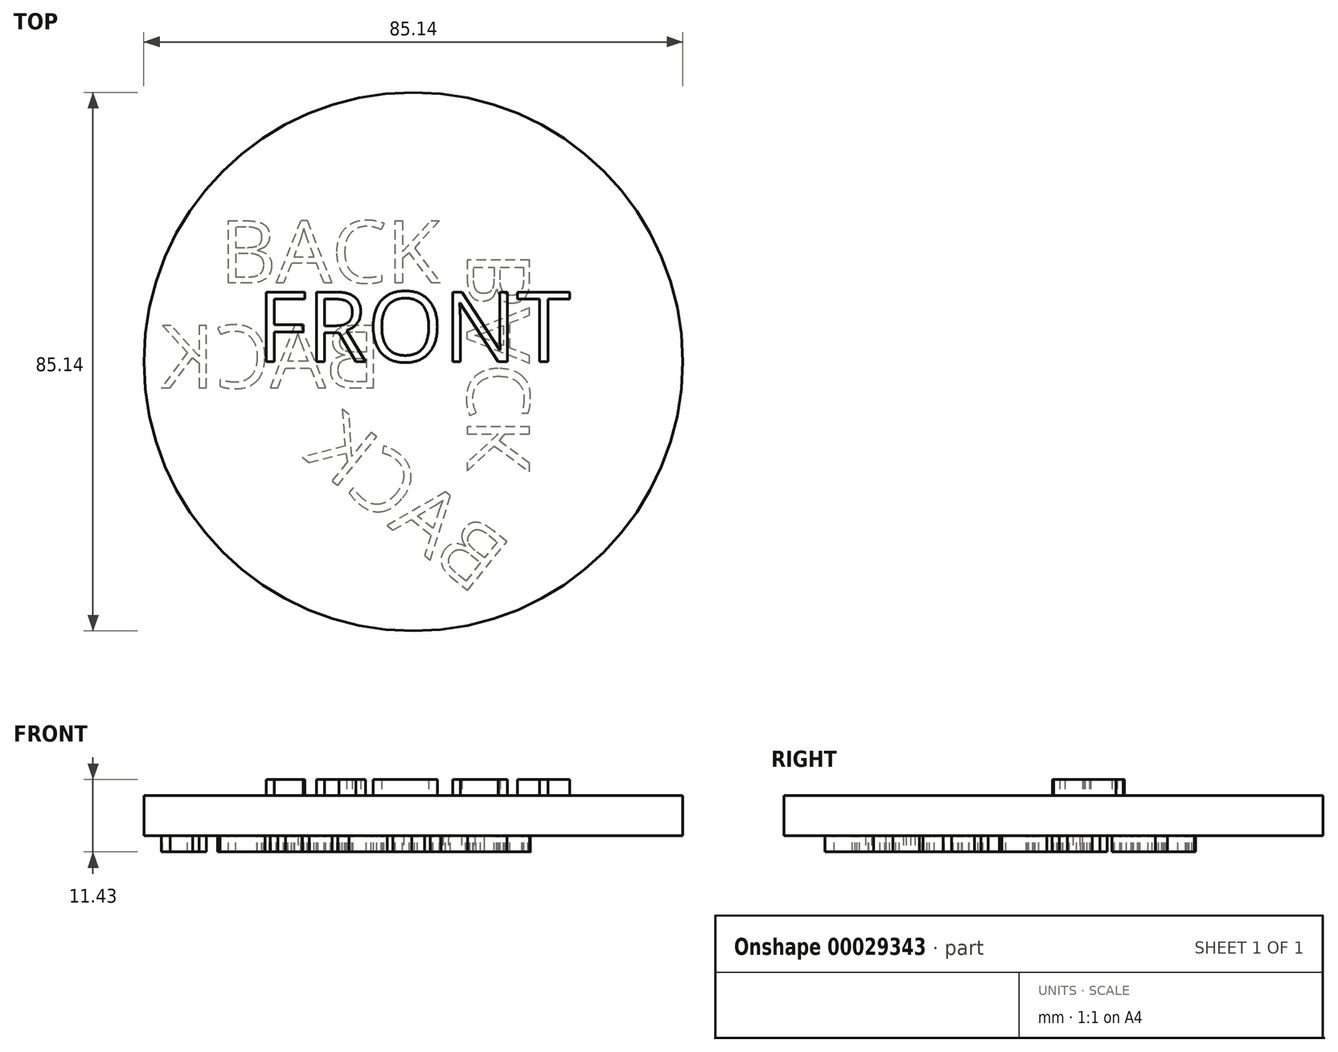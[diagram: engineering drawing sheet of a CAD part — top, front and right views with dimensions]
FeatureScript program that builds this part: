
annotation { "Feature Type Name" : "Feature", "Feature Type Description" : "" }
export const myFeature = defineFeature(function(context is Context, id is Id, definition is map)
    precondition{}
    {
        {
            var Q0;
            Q0=qCreatedBy(makeId("Top.planeOp"),FACE);
            var sketch = newSketch(context, id + "F0", { "sketchPlane" : qUnion([Q0])});
            skCircle(sketch, "E0", {"center": v(0, 0) * mm, "radius": 42.57 * mm});
            skSolve(sketch);
        }
        {
            var Q0;
            Q0=makeQuery(id+"F0.imprint","IMPRINT",FACE,{"disambiguationData":[TD([[makeQuery(id+"F0.imprint","IMPRINT",EDGE,{"derivedFrom":sQuery(id+"F0.wireOp",EDGE,"E0")}),1.0]])]});
            extrude(context, id + "F1", {"entities" : qUnion([Q0]), "depth" : 6.35 * mm});
        }
        {
            var Q0;
            Q0=makeQuery(id+"F1.opExtrude","CAP_FACE",FACE,{"disambiguationData":[OSD([sQuery(id+"F0.wireOp",EDGE,"E0")])],"isStart":false});
            var sketch = newSketch(context, id + "F2", { "sketchPlane" : qUnion([Q0])});
            skText(sketch, "E1", { "text": "FRONT", "fontName": "OpenSans-Regular.ttf"});
            const initialGuessF2  = {"E1": [-0.02476, 0, 1, 0, 0.0111]};
            skSetInitialGuess(sketch, initialGuessF2);
            skSolve(sketch);
        }
        {
            var Q0;
            Q0=qSketchRegion(id+"F2",true);
            extrude(context, id + "F3", {"entities" : qUnion([Q0]), "operationType" : NewBodyOperationType.ADD, "depth" : 2.54 * mm});
        }
        {
            var Q0;
            Q0=makeQuery(id+"F1.opExtrude","CAP_FACE",FACE,{"disambiguationData":[OSD([sQuery(id+"F0.wireOp",EDGE,"E0")])],"isStart":true});
            var sketch = newSketch(context, id + "F4", { "sketchPlane" : qUnion([Q0])});
            skText(sketch, "E2", { "text": "BACK", "fontName": "OpenSans-Regular.ttf"});
            skText(sketch, "E3", { "text": "BACK", "fontName": "OpenSans-Regular.ttf"});
            skText(sketch, "E4", { "text": "BACK", "fontName": "OpenSans-Regular.ttf"});
            const initialGuessF4  = {"E2": [-0.00492, 0.00414, -1, 0, 0.00994], "E3": [0.01838, -0.01744, 0, 1, 0.00994], "E4": [0.00965, 0.03698, -0.77875, -0.62733, 0.00994]};
            skSetInitialGuess(sketch, initialGuessF4);
            skSolve(sketch);
        }
        {
            var Q0;
            Q0=qSketchRegion(id+"F4",true);
            extrude(context, id + "F5", {"entities" : qUnion([Q0]), "operationType" : NewBodyOperationType.ADD, "depth" : 2.54 * mm});
        }
        {
            var Q0;
            {var subQ0=sQuery(id+"F0.wireOp",EDGE,"E0");Q0=makeQuery(id+"F3.boolean.opBoolean","SPLIT",FACE,{"disambiguationData":[TD([makeQuery(id+"F1.opExtrude","SWEPT_FACE",FACE,{"disambiguationData":[OSD([subQ0])]})])],"derivedFrom":makeQuery(id+"F1.opExtrude","CAP_FACE",FACE,{"disambiguationData":[OSD([subQ0])],"isStart":false})});}
            var sketch = newSketch(context, id + "F6", { "sketchPlane" : qUnion([Q0])});
            skText(sketch, "E5", { "text": "BACK\n", "fontName": "OpenSans-Regular.ttf"});
            const initialGuessF6  = {"E5": [-0.03058, 0.01242, 1, 0, 0.00994]};
            skSetInitialGuess(sketch, initialGuessF6);
            skSolve(sketch);
        }
        {
            var Q0;
            Q0 = qSketchRegion(id + "F6", true);
            var Q1;
            Q1=makeQuery(id+"F5.opExtrude","CAP_FACE",FACE,{"disambiguationData":[OSD([sQuery(id+"F4.wireOp",EDGE,"E2.sketch_text.stroke-0"),sQuery(id+"F4.wireOp",EDGE,"E2.sketch_text.stroke-1"),sQuery(id+"F4.wireOp",EDGE,"E2.sketch_text.stroke-2"),sQuery(id+"F4.wireOp",EDGE,"E2.sketch_text.stroke-3"),sQuery(id+"F4.wireOp",EDGE,"E2.sketch_text.stroke-4"),sQuery(id+"F4.wireOp",EDGE,"E2.sketch_text.stroke-5"),sQuery(id+"F4.wireOp",EDGE,"E2.sketch_text.stroke-6"),sQuery(id+"F4.wireOp",EDGE,"E2.sketch_text.stroke-7"),sQuery(id+"F4.wireOp",EDGE,"E2.sketch_text.stroke-8"),sQuery(id+"F4.wireOp",EDGE,"E2.sketch_text.stroke-9"),sQuery(id+"F4.wireOp",EDGE,"E2.sketch_text.stroke-10"),sQuery(id+"F4.wireOp",EDGE,"E2.sketch_text.stroke-11"),sQuery(id+"F4.wireOp",EDGE,"E2.sketch_text.stroke-12"),sQuery(id+"F4.wireOp",EDGE,"E2.sketch_text.stroke-13"),sQuery(id+"F4.wireOp",EDGE,"E2.sketch_text.stroke-14"),sQuery(id+"F4.wireOp",EDGE,"E2.sketch_text.stroke-15"),sQuery(id+"F4.wireOp",EDGE,"E2.sketch_text.stroke-16"),sQuery(id+"F4.wireOp",EDGE,"E2.sketch_text.stroke-17"),sQuery(id+"F4.wireOp",EDGE,"E2.sketch_text.stroke-18"),sQuery(id+"F4.wireOp",EDGE,"E2.sketch_text.stroke-19"),sQuery(id+"F4.wireOp",EDGE,"E2.sketch_text.stroke-20"),sQuery(id+"F4.wireOp",EDGE,"E2.sketch_text.stroke-21"),sQuery(id+"F4.wireOp",EDGE,"E2.sketch_text.stroke-22"),sQuery(id+"F4.wireOp",EDGE,"E2.sketch_text.stroke-23"),sQuery(id+"F4.wireOp",EDGE,"E2.sketch_text.stroke-24")])],"isStart":false});
            extrude(context, id + "F7", {"entities" : qUnion([Q0]), "operationType" : NewBodyOperationType.ADD, "endBound" : BoundingType.UP_TO_SURFACE, "oppositeDirection" : true, "endBoundEntityFace" : qUnion([Q1]), "depth" : 25.4 * mm});
        }
    });
